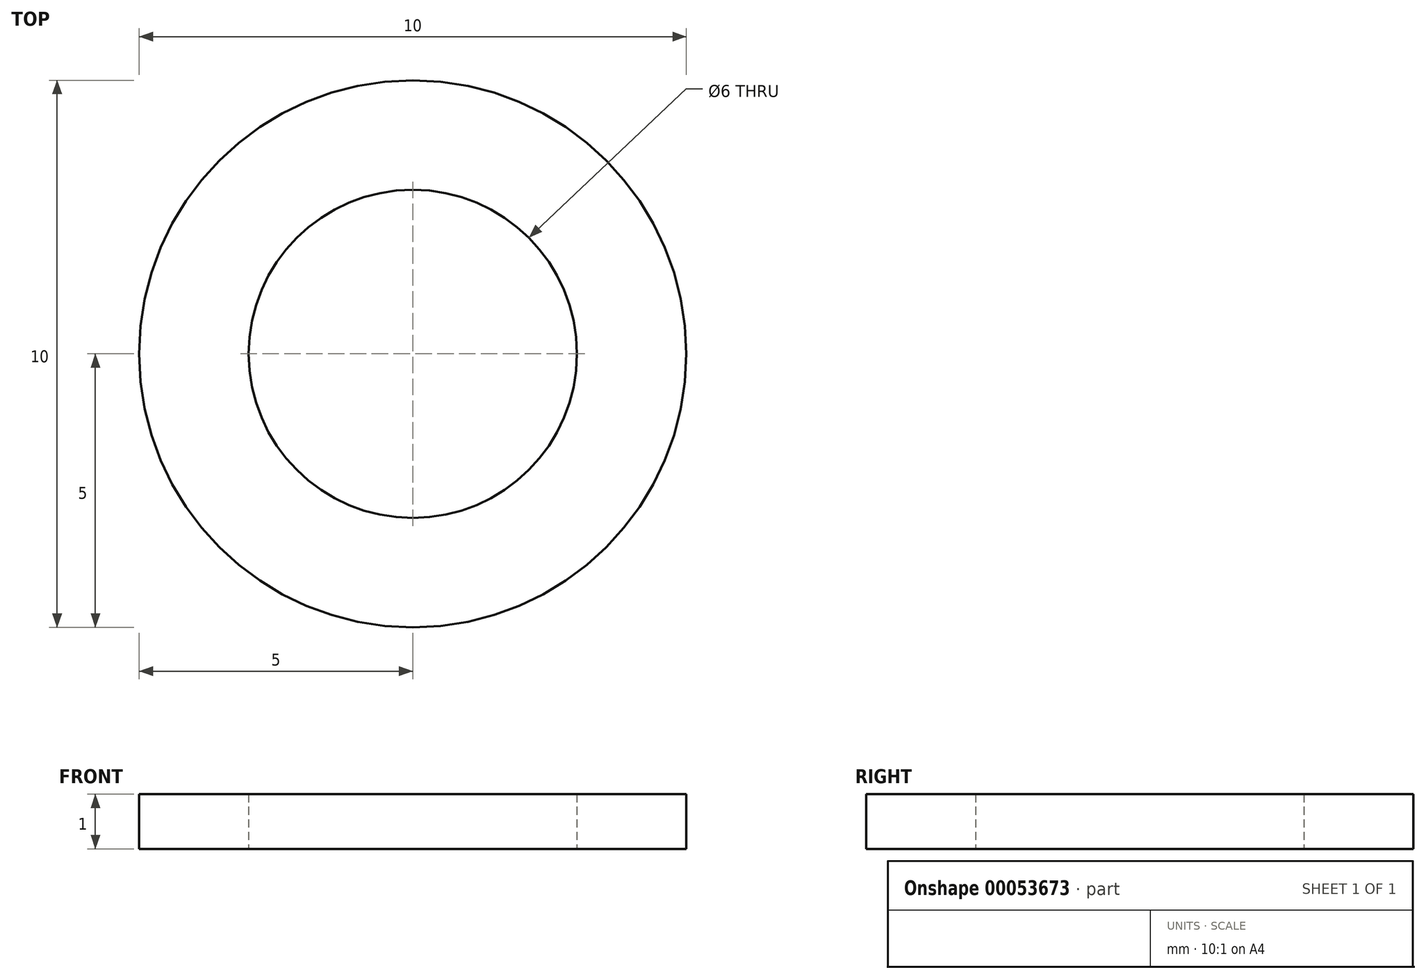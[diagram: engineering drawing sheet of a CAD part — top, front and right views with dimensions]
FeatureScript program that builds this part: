
annotation { "Feature Type Name" : "Feature", "Feature Type Description" : "" }
export const myFeature = defineFeature(function(context is Context, id is Id, definition is map)
    precondition{}
    {
        {
            var Q0;
            Q0=qCreatedBy(makeId("Top.planeOp"),FACE);
            var sketch = newSketch(context, id + "F0", { "sketchPlane" : qUnion([Q0])});
            skCircle(sketch, "E0", {"center": v(0, 0) * mm, "radius": 3 * mm});
            skCircle(sketch, "E1", {"center": v(0, 0) * mm, "radius": 5 * mm});
            skSolve(sketch);
        }
        {
            var Q0;
            Q0=makeQuery(id+"F0.imprint","IMPRINT",FACE,{"disambiguationData":[TD([[makeQuery(id+"F0.imprint","IMPRINT",EDGE,{"derivedFrom":sQuery(id+"F0.wireOp",EDGE,"E0")}),-1.0]])]});
            extrude(context, id + "F1", {"entities" : qUnion([Q0]), "depth" : 1 * mm});
        }
    });
